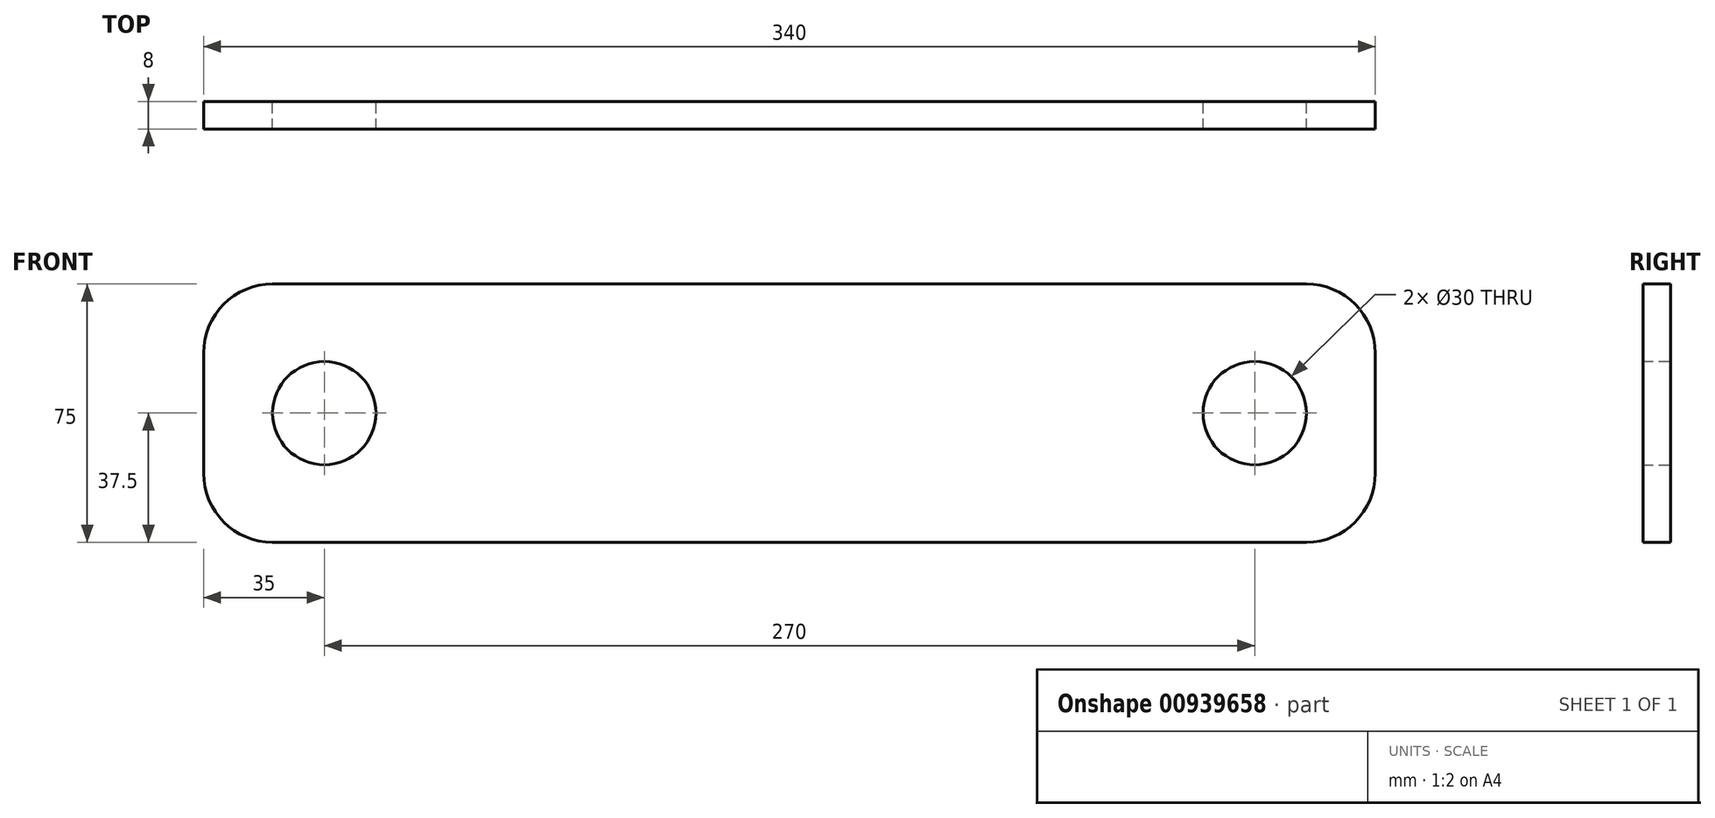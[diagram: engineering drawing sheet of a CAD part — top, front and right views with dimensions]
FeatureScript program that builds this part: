
annotation { "Feature Type Name" : "Feature", "Feature Type Description" : "" }
export const myFeature = defineFeature(function(context is Context, id is Id, definition is map)
    precondition{}
    {
        {
            var Q0;
            Q0=qCreatedBy(makeId("Front.planeOp"),FACE);
            var sketch = newSketch(context, id + "F0", { "sketchPlane" : qUnion([Q0])});
            skLineSegment(sketch, "E0.bottom", {"start": v(170, -37.5) * mm, "end": v(-170, -37.5) * mm});
            skLineSegment(sketch, "E0.top", {"start": v(170, 37.5) * mm, "end": v(-170, 37.5) * mm});
            skLineSegment(sketch, "E0.left", {"start": v(170, -37.5) * mm, "end": v(170, 37.5) * mm});
            skLineSegment(sketch, "E0.right", {"start": v(-170, -37.5) * mm, "end": v(-170, 37.5) * mm});
            skPoint(sketch, "E0.middle", {"position": v(0, 0) * mm});
            skCircle(sketch, "E1", {"center": v(135, 0) * mm, "radius": 15 * mm});
            skCircle(sketch, "E2", {"center": v(-135, 0) * mm, "radius": 15 * mm});
            skSolve(sketch);
        }
        {
            var Q0;
            Q0=makeQuery(id+"F0.imprint","IMPRINT",FACE,{"disambiguationData":[TD([[makeQuery(id+"F0.imprint","IMPRINT",EDGE,{"derivedFrom":sQuery(id+"F0.wireOp",EDGE,"E0.bottom")}),-1.0]])]});
            extrude(context, id + "F1", {"entities" : qUnion([Q0]), "depth" : 8 * mm, "offsetDistance" : 25 * mm});
        }
        {
            var Q0;
            Q0=makeQuery(id+"F1.opExtrude","SWEPT_EDGE",EDGE,{"disambiguationData":[OSD([sQuery(id+"F0.wireOp",EDGE,"E0.top"),sQuery(id+"F0.wireOp",EDGE,"E0.right")])]});
            var Q1;
            Q1=makeQuery(id+"F1.opExtrude","SWEPT_EDGE",EDGE,{"disambiguationData":[OSD([sQuery(id+"F0.wireOp",EDGE,"E0.bottom"),sQuery(id+"F0.wireOp",EDGE,"E0.right")])]});
            var Q2;
            Q2=makeQuery(id+"F1.opExtrude","SWEPT_EDGE",EDGE,{"disambiguationData":[OSD([sQuery(id+"F0.wireOp",EDGE,"E0.bottom"),sQuery(id+"F0.wireOp",EDGE,"E0.left")])]});
            var Q3;
            Q3=makeQuery(id+"F1.opExtrude","SWEPT_EDGE",EDGE,{"disambiguationData":[OSD([sQuery(id+"F0.wireOp",EDGE,"E0.top"),sQuery(id+"F0.wireOp",EDGE,"E0.left")])]});
            fillet(context, id + "F2", {"entities" : qUnion([Q0, Q1, Q2, Q3]), "radius" : 20 * mm, "tangentPropagation" : true, "allowEdgeOverflow" : false});
        }
    });
